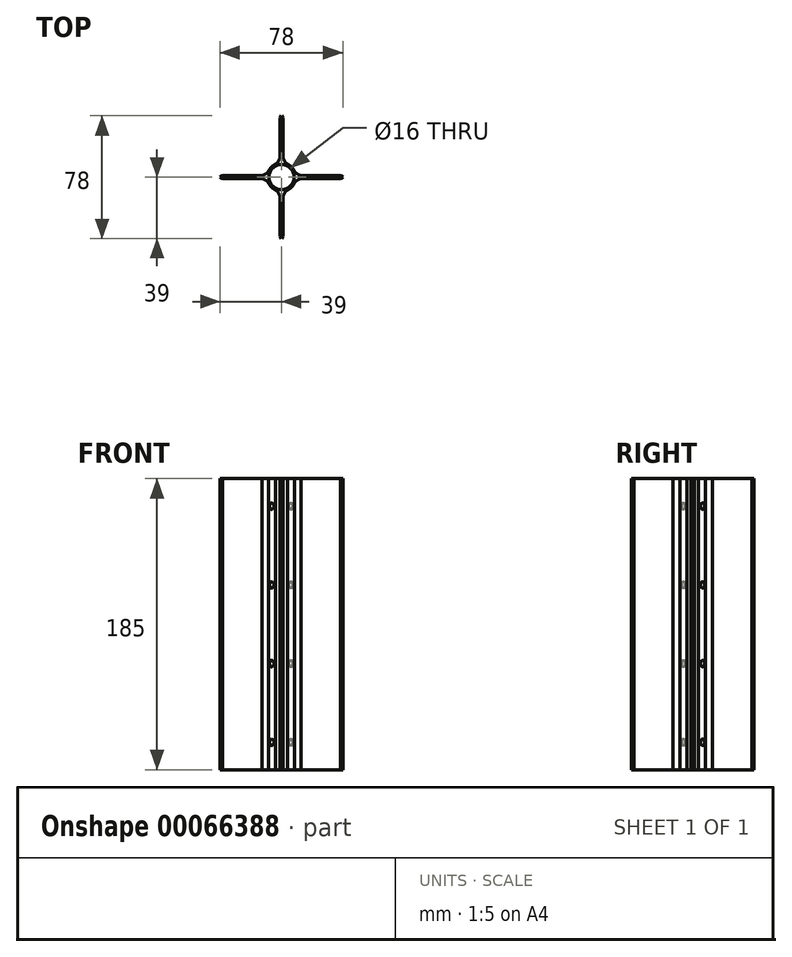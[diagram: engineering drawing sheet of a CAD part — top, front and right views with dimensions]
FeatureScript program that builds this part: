
annotation { "Feature Type Name" : "Feature", "Feature Type Description" : "" }
export const myFeature = defineFeature(function(context is Context, id is Id, definition is map)
    precondition{}
    {
        {
            var Q0;
            Q0=qCreatedBy(makeId("Top.planeOp"),FACE);
            var sketch = newSketch(context, id + "F0", { "sketchPlane" : qUnion([Q0])});
            skCircle(sketch, "E0", {"center": v(0, 0) * mm, "radius": 8 * mm});
            skLineSegment(sketch, "E1", {"start": v(0, 0) * mm, "end": v(-1, 0) * mm, "construction": true});
            skPoint(sketch, "E2.startSnap0", {"position": v(-0.5, 0) * mm});
            skLineSegment(sketch, "E3", {"start": v(0, 0) * mm, "end": v(0, 9) * mm, "construction": true});
            skLineSegment(sketch, "E4", {"start": v(0, 9) * mm, "end": v(0, 39) * mm, "construction": true});
            skLineSegment(sketch, "E5", {"start": v(-1, 12.46) * mm, "end": v(-1, 37.46) * mm});
            skLineSegment(sketch, "E6", {"start": v(-1, 37.46) * mm, "end": v(0, 39) * mm});
            skLineSegment(sketch, "E7.MirrorCS", {"start": v(1, 12.46) * mm, "end": v(1, 37.46) * mm});
            skLineSegment(sketch, "E8.MirrorCS", {"start": v(1, 37.46) * mm, "end": v(0, 39) * mm});
            skArc(sketch, "E9", {"start": v(-3.67, 8.22) * mm, "mid": v(-1.95, 10.1) * mm, "end": v(-1, 12.46) * mm});
            skArc(sketch, "E10.MirrorCS", {"start": v(3.67, 8.22) * mm, "mid": v(1.95, 10.1) * mm, "end": v(1, 12.46) * mm});
            skPoint(sketch, "E11.orphan", {"position": v(-1, 8.94) * mm});
            skPoint(sketch, "E12.orphan", {"position": v(1, 8.94) * mm});
            skArc(sketch, "E13.trimOffspring", {"start": v(-3.67, 8.22) * mm, "mid": v(-6.36, 6.36) * mm, "end": v(-8.22, 3.67) * mm});
            skLineSegment(sketch, "E14.1.0", {"start": v(-37.46, 1) * mm, "end": v(-39, 0) * mm});
            skLineSegment(sketch, "E14.1.1", {"start": v(-12.46, 1) * mm, "end": v(-37.46, 1) * mm});
            skPoint(sketch, "E14.1.2", {"position": v(-8.94, 1) * mm});
            skLineSegment(sketch, "E14.1.3", {"start": v(-37.46, -1) * mm, "end": v(-39, 0) * mm});
            skPoint(sketch, "E14.1.4", {"position": v(-8.94, -1) * mm});
            skLineSegment(sketch, "E14.1.5", {"start": v(-9, 0) * mm, "end": v(-39, 0) * mm, "construction": true});
            skLineSegment(sketch, "E14.1.6", {"start": v(-12.46, -1) * mm, "end": v(-37.46, -1) * mm});
            skArc(sketch, "E14.1.7", {"start": v(-8.22, -3.67) * mm, "mid": v(-10.1, -1.95) * mm, "end": v(-12.46, -1) * mm});
            skArc(sketch, "E14.1.8", {"start": v(-8.22, 3.67) * mm, "mid": v(-10.1, 1.95) * mm, "end": v(-12.46, 1) * mm});
            skLineSegment(sketch, "E14.2.0", {"start": v(-1, -37.46) * mm, "end": v(0, -39) * mm});
            skLineSegment(sketch, "E14.2.1", {"start": v(-1, -12.46) * mm, "end": v(-1, -37.46) * mm});
            skPoint(sketch, "E14.2.2", {"position": v(-1, -8.94) * mm});
            skLineSegment(sketch, "E14.2.3", {"start": v(1, -37.46) * mm, "end": v(0, -39) * mm});
            skPoint(sketch, "E14.2.4", {"position": v(1, -8.94) * mm});
            skLineSegment(sketch, "E14.2.5", {"start": v(0, -9) * mm, "end": v(0, -39) * mm, "construction": true});
            skLineSegment(sketch, "E14.2.6", {"start": v(1, -12.46) * mm, "end": v(1, -37.46) * mm});
            skArc(sketch, "E14.2.7", {"start": v(3.67, -8.22) * mm, "mid": v(1.95, -10.1) * mm, "end": v(1, -12.46) * mm});
            skArc(sketch, "E14.2.8", {"start": v(-3.67, -8.22) * mm, "mid": v(-1.95, -10.1) * mm, "end": v(-1, -12.46) * mm});
            skArc(sketch, "E15.trimOffspring", {"start": v(-8.22, -3.67) * mm, "mid": v(-6.36, -6.36) * mm, "end": v(-3.67, -8.22) * mm});
            skArc(sketch, "E16.trimOffspring", {"start": v(8.22, 3.67) * mm, "mid": v(6.36, 6.36) * mm, "end": v(3.67, 8.22) * mm});
            skLineSegment(sketch, "E17.1.3.0", {"start": v(37.46, -1) * mm, "end": v(39, 0) * mm});
            skLineSegment(sketch, "E17.3.3.0", {"start": v(12.46, -1) * mm, "end": v(37.46, -1) * mm});
            skPoint(sketch, "E17.6.3.0", {"position": v(8.94, -1) * mm});
            skLineSegment(sketch, "E17.7.3.0", {"start": v(37.46, 1) * mm, "end": v(39, 0) * mm});
            skPoint(sketch, "E17.10.3.0", {"position": v(8.94, 1) * mm});
            skLineSegment(sketch, "E17.11.3.0", {"start": v(9, 0) * mm, "end": v(39, 0) * mm, "construction": true});
            skLineSegment(sketch, "E17.14.3.0", {"start": v(12.46, 1) * mm, "end": v(37.46, 1) * mm});
            skArc(sketch, "E17.17.3.0", {"start": v(8.22, 3.67) * mm, "mid": v(10.1, 1.95) * mm, "end": v(12.46, 1) * mm});
            skArc(sketch, "E17.21.3.0", {"start": v(8.22, -3.67) * mm, "mid": v(10.1, -1.95) * mm, "end": v(12.46, -1) * mm});
            skArc(sketch, "E18.trimOffspring", {"start": v(3.67, -8.22) * mm, "mid": v(6.36, -6.36) * mm, "end": v(8.22, -3.67) * mm});
            skLineSegment(sketch, "E19", {"start": v(84.06, -1) * mm, "end": v(-81.4, 0) * mm, "construction": true});
            skSolve(sketch);
        }
        {
            var Q0;
            Q0=makeQuery(id+"F0.imprint","IMPRINT",FACE,{"disambiguationData":[TD([[makeQuery(id+"F0.imprint","IMPRINT",EDGE,{"derivedFrom":sQuery(id+"F0.wireOp",EDGE,"E0")}),-1.0]])]});
            extrude(context, id + "F1", {"entities" : qUnion([Q0]), "depth" : 185 * mm});
        }
        {
            var Q0;
            Q0=qCreatedBy(makeId("Right.planeOp"),FACE);
            var sketch = newSketch(context, id + "F2", { "sketchPlane" : qUnion([Q0])});
            skLineSegment(sketch, "E20", {"start": v(0, -53.4) * mm, "end": v(0, 236.7) * mm, "construction": true});
            skSolve(sketch);
        }
        {
            var Q0;
            Q0=qCreatedBy(makeId("Right.planeOp"),FACE);
            var Q1;
            Q1=sQuery(id+"F2.wireOp",EDGE,"E20");
            cPlane(context, id + "F3", {"entities" : qUnion([Q0, Q1]), "cplaneType" : CPlaneType.LINE_ANGLE, "offset" : 150 * mm, "angle" : 45 * degree, "width" : 150 * mm, "height" : 150 * mm});
        }
        {
            var Q0;
            Q0=qCreatedBy(id+"F3.planeOp",FACE);
            cPlane(context, id + "F4", {"entities" : qUnion([Q0]), "cplaneType" : CPlaneType.OFFSET, "offset" : 9 * mm, "width" : 150 * mm, "height" : 150 * mm});
        }
        {
            var Q0;
            Q0=qCreatedBy(id+"F4.planeOp",FACE);
            var sketch = newSketch(context, id + "F5", { "sketchPlane" : qUnion([Q0])});
            skLineSegment(sketch, "E21", {"start": v(0, 0) * mm, "end": v(0, 200) * mm, "construction": true});
            skCircle(sketch, "E22", {"center": v(0, 17.5) * mm, "radius": 2 * mm});
            skCircle(sketch, "E23.0.1.0", {"center": v(0, 67.5) * mm, "radius": 2 * mm});
            skCircle(sketch, "E23.0.2.0", {"center": v(0, 117.5) * mm, "radius": 2 * mm});
            skCircle(sketch, "E23.0.3.0", {"center": v(0, 167.5) * mm, "radius": 2 * mm});
            skLineSegment(sketch, "E23.direction1", {"start": v(0, 17.5) * mm, "end": v(25, 17.5) * mm, "construction": true});
            skLineSegment(sketch, "E23.direction2", {"start": v(0, 17.5) * mm, "end": v(0, 67.5) * mm, "construction": true});
            skSolve(sketch);
        }
        {
            var Q0;
            Q0=makeQuery(id+"F5.imprint","IMPRINT",FACE,{"disambiguationData":[TD([[makeQuery(id+"F5.imprint","IMPRINT",EDGE,{"derivedFrom":sQuery(id+"F5.wireOp",EDGE,"E22")}),1.0]])]});
            var Q1;
            Q1=makeQuery(id+"F5.imprint","IMPRINT",FACE,{"disambiguationData":[TD([[makeQuery(id+"F5.imprint","IMPRINT",EDGE,{"derivedFrom":sQuery(id+"F5.wireOp",EDGE,"E23.0.1.0")}),1.0]])]});
            var Q2;
            Q2=makeQuery(id+"F5.imprint","IMPRINT",FACE,{"disambiguationData":[TD([[makeQuery(id+"F5.imprint","IMPRINT",EDGE,{"derivedFrom":sQuery(id+"F5.wireOp",EDGE,"E23.0.2.0")}),1.0]])]});
            var Q3;
            Q3=makeQuery(id+"F5.imprint","IMPRINT",FACE,{"disambiguationData":[TD([[makeQuery(id+"F5.imprint","IMPRINT",EDGE,{"derivedFrom":sQuery(id+"F5.wireOp",EDGE,"E23.0.3.0")}),1.0]])]});
            extrude(context, id + "F6", {"entities" : qUnion([Q0, Q1, Q2, Q3]), "operationType" : NewBodyOperationType.REMOVE, "oppositeDirection" : true, "depth" : 100 * mm});
        }
    });
